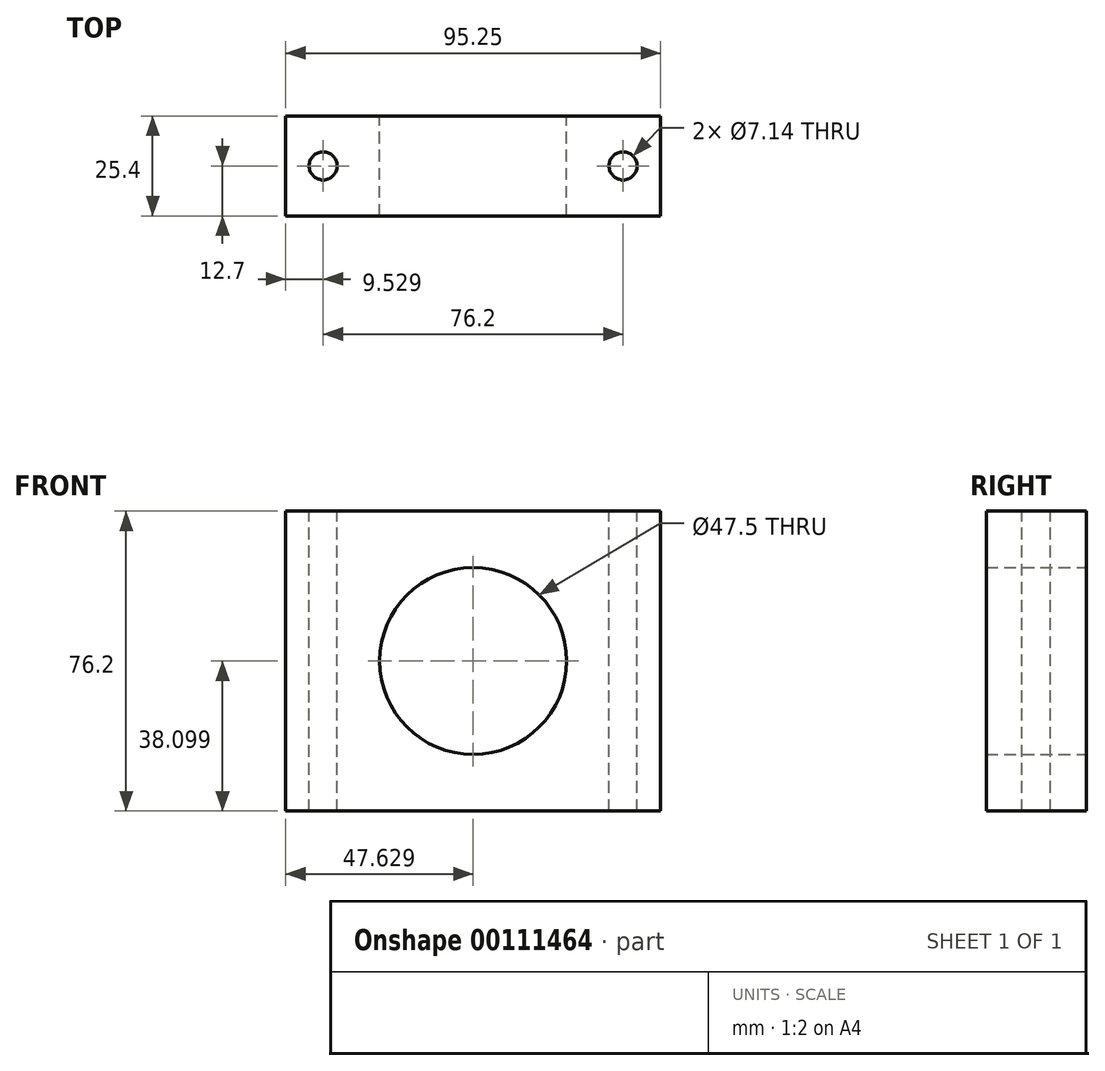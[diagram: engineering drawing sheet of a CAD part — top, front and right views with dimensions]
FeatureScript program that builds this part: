
annotation { "Feature Type Name" : "Feature", "Feature Type Description" : "" }
export const myFeature = defineFeature(function(context is Context, id is Id, definition is map)
    precondition{}
    {
        {
            var Q0;
            Q0=qCreatedBy(makeId("Front.planeOp"),FACE);
            var sketch = newSketch(context, id + "F0", { "sketchPlane" : qUnion([Q0])});
            skLineSegment(sketch, "E0", {"start": v(-37.07, 40.39) * mm, "end": v(-37.07, -35.81) * mm});
            skLineSegment(sketch, "E1", {"start": v(-37.07, -35.81) * mm, "end": v(58.18, -35.81) * mm});
            skLineSegment(sketch, "E2", {"start": v(58.18, -35.81) * mm, "end": v(58.18, 40.39) * mm});
            skLineSegment(sketch, "E3", {"start": v(58.18, 40.39) * mm, "end": v(-37.07, 40.39) * mm});
            skLineSegment(sketch, "E4", {"start": v(10.56, 40.39) * mm, "end": v(10.56, -35.81) * mm, "construction": true});
            skLineSegment(sketch, "E5", {"start": v(58.18, 2.29) * mm, "end": v(-37.07, 2.29) * mm, "construction": true});
            skCircle(sketch, "E6", {"center": v(10.56, 2.29) * mm, "radius": 23.75 * mm});
            skSolve(sketch);
        }
        {
            var Q0;
            Q0=makeQuery(id+"F0.imprint","IMPRINT",FACE,{"disambiguationData":[TD([[makeQuery(id+"F0.imprint","IMPRINT",EDGE,{"derivedFrom":sQuery(id+"F0.wireOp",EDGE,"E0")}),1.0]])]});
            extrude(context, id + "F1", {"entities" : qUnion([Q0]), "depth" : 25.4 * mm});
        }
        {
            var Q0;
            Q0=makeQuery(id+"F1.opExtrude","SWEPT_FACE",FACE,{"disambiguationData":[OSD([sQuery(id+"F0.wireOp",EDGE,"E3")])]});
            var sketch = newSketch(context, id + "F2", { "sketchPlane" : qUnion([Q0])});
            skCircle(sketch, "E7", {"center": v(-27.54, -12.7) * mm, "radius": 3.57 * mm});
            skPoint(sketch, "E7.centerSnap0", {"position": v(-37.07, -12.7) * mm});
            skCircle(sketch, "E8", {"center": v(48.66, -12.7) * mm, "radius": 3.57 * mm});
            skPoint(sketch, "E8.centerSnap0", {"position": v(58.18, -12.7) * mm});
            skSolve(sketch);
        }
        {
            var Q0;
            Q0=makeQuery(id+"F2.imprint","IMPRINT",FACE,{"disambiguationData":[TD([[makeQuery(id+"F2.imprint","IMPRINT",EDGE,{"derivedFrom":sQuery(id+"F2.wireOp",EDGE,"E8")}),1.0]])]});
            var Q1;
            Q1=makeQuery(id+"F2.imprint","IMPRINT",FACE,{"disambiguationData":[TD([[makeQuery(id+"F2.imprint","IMPRINT",EDGE,{"derivedFrom":sQuery(id+"F2.wireOp",EDGE,"E7")}),1.0]])]});
            extrude(context, id + "F3", {"entities" : qUnion([Q0, Q1]), "operationType" : NewBodyOperationType.REMOVE, "endBound" : BoundingType.THROUGH_ALL, "oppositeDirection" : true, "depth" : 25.4 * mm});
        }
    });
